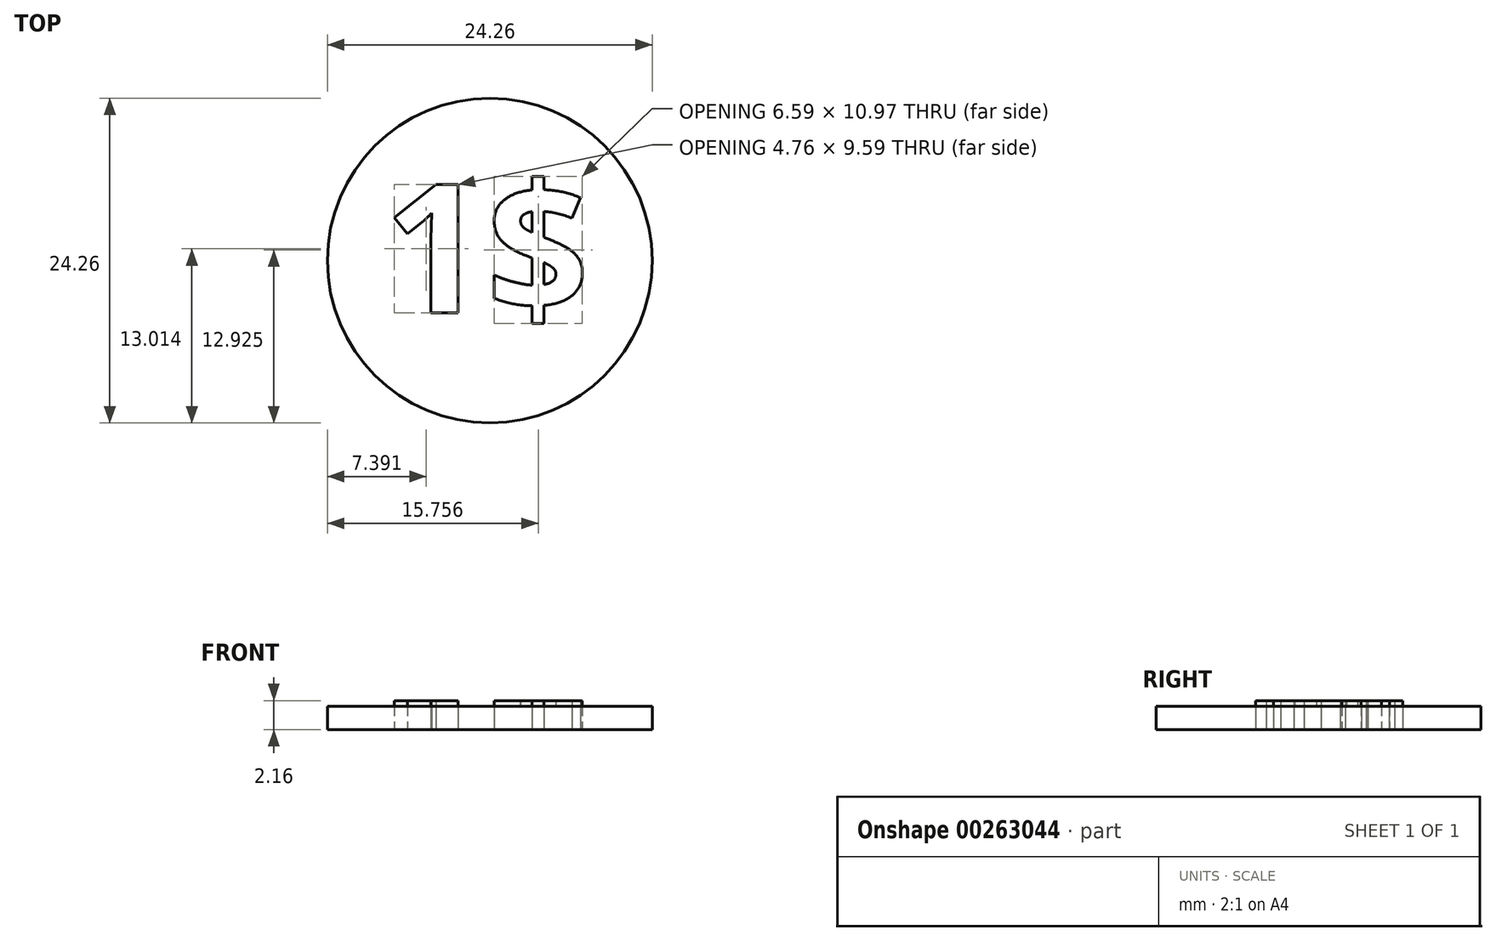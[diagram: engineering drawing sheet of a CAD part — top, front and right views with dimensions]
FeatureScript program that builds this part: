
annotation { "Feature Type Name" : "Feature", "Feature Type Description" : "" }
export const myFeature = defineFeature(function(context is Context, id is Id, definition is map)
    precondition{}
    {
        {
            var Q0;
            Q0=qCreatedBy(makeId("Top.planeOp"),FACE);
            var sketch = newSketch(context, id + "F0", { "sketchPlane" : qUnion([Q0])});
            skCircle(sketch, "E0", {"center": v(0, 0) * mm, "radius": 12.13 * mm});
            skText(sketch, "E1", { "text": "1$", "fontName": "OpenSans-Bold.ttf"});
            const initialGuessF0  = {"E1": [-0.00791, -0.00391, 1, 0, 0.00967]};
            skSetInitialGuess(sketch, initialGuessF0);
            skSolve(sketch);
        }
        {
            var Q0;
            Q0=makeQuery(id+"F0.imprint","IMPRINT",FACE,{"disambiguationData":[TD([[makeQuery(id+"F0.imprint","IMPRINT",EDGE,{"derivedFrom":sQuery(id+"F0.wireOp",EDGE,"E1.sketch_text.stroke-0")}),-1.0]])]});
            extrude(context, id + "F1", {"entities" : qUnion([Q0]), "depth" : 2.16 * mm});
        }
        {
            var Q0;
            Q0=makeQuery(id+"F0.imprint","IMPRINT",FACE,{"disambiguationData":[TD([[makeQuery(id+"F0.imprint","IMPRINT",EDGE,{"derivedFrom":sQuery(id+"F0.wireOp",EDGE,"E1.sketch_text.stroke-10")}),-1.0]])]});
            extrude(context, id + "F2", {"entities" : qUnion([Q0]), "depth" : 2.16 * mm});
        }
        {
            var Q0;
            Q0=makeQuery(id+"F0.imprint","IMPRINT",FACE,{"disambiguationData":[TD([[makeQuery(id+"F0.imprint","IMPRINT",EDGE,{"derivedFrom":sQuery(id+"F0.wireOp",EDGE,"E1.sketch_text.stroke-39")}),1.0]])]});
            extrude(context, id + "F3", {"entities" : qUnion([Q0]), "operationType" : NewBodyOperationType.ADD, "depth" : 1.75 * mm});
        }
        {
            var Q0;
            Q0=makeQuery(id+"F0.imprint","IMPRINT",FACE,{"disambiguationData":[TD([[makeQuery(id+"F0.imprint","IMPRINT",EDGE,{"derivedFrom":sQuery(id+"F0.wireOp",EDGE,"E1.sketch_text.stroke-35")}),1.0]])]});
            extrude(context, id + "F4", {"entities" : qUnion([Q0]), "operationType" : NewBodyOperationType.ADD, "depth" : 1.75 * mm});
        }
        {
            var Q0;
            Q0=makeQuery(id+"F0.imprint","IMPRINT",FACE,{"disambiguationData":[TD([[makeQuery(id+"F0.imprint","IMPRINT",EDGE,{"derivedFrom":sQuery(id+"F0.wireOp",EDGE,"E0")}),1.0]])]});
            extrude(context, id + "F5", {"entities" : qUnion([Q0]), "depth" : 1.75 * mm});
        }
    });
